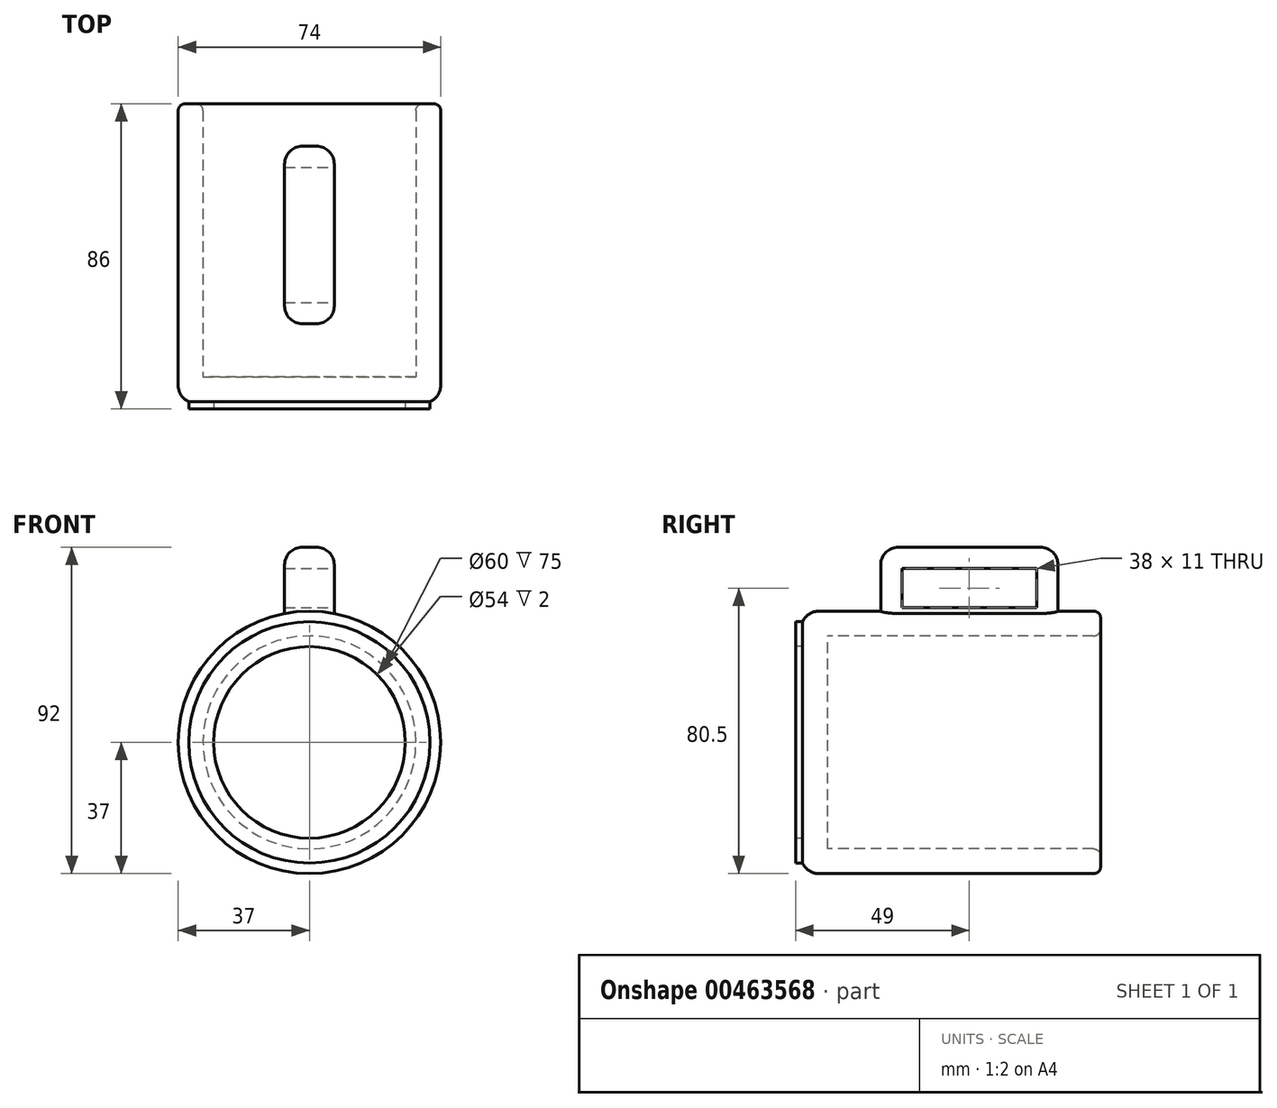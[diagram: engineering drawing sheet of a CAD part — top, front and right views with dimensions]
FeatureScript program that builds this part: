
annotation { "Feature Type Name" : "Feature", "Feature Type Description" : "" }
export const myFeature = defineFeature(function(context is Context, id is Id, definition is map)
    precondition{}
    {
        {
            var Q0;
            Q0=qCreatedBy(makeId("Top.planeOp"),FACE);
            var sketch = newSketch(context, id + "F0", { "sketchPlane" : qUnion([Q0])});
            skLineSegment(sketch, "E0", {"start": v(0, 0) * mm, "end": v(-30, 0) * mm});
            skLineSegment(sketch, "E1", {"start": v(-30, 0) * mm, "end": v(-30, 77) * mm});
            skLineSegment(sketch, "E2", {"start": v(-30, 77) * mm, "end": v(-37, 77) * mm});
            skLineSegment(sketch, "E3.0", {"start": v(-37, -7) * mm, "end": v(-37, 77) * mm});
            skLineSegment(sketch, "E3.1", {"start": v(0, -7) * mm, "end": v(-27, -7) * mm});
            skLineSegment(sketch, "E4", {"start": v(0, -7) * mm, "end": v(0, 0) * mm});
            skLineSegment(sketch, "E5", {"start": v(-37, -7) * mm, "end": v(-34, -7) * mm});
            skLineSegment(sketch, "E6", {"start": v(-34, -7) * mm, "end": v(-34, -9) * mm});
            skLineSegment(sketch, "E7", {"start": v(-34, -9) * mm, "end": v(-27, -9) * mm});
            skLineSegment(sketch, "E8", {"start": v(-27, -9) * mm, "end": v(-27, -7) * mm});
            skLineSegment(sketch, "E9.trimOffspring", {"start": v(-34, -7) * mm, "end": v(-37, -7) * mm});
            skLineSegment(sketch, "E10", {"start": v(0, 0) * mm, "end": v(0, 77) * mm});
            skSolve(sketch);
        }
        {
            var Q0;
            Q0 = qSketchRegion(id + "F0", true);
            var Q1;
            Q1=sQuery(id+"F0.wireOp",EDGE,"E10");
            revolve(context, id + "F1", {"entities" : qUnion([Q0]), "axis" : qUnion([Q1]), "revolveType" : RevolveType.FULL});
        }
        {
            var Q0;
            Q0=makeQuery(id+"F1.opRevolve","SWEPT_EDGE",EDGE,{"disambiguationData":[OSD([sQuery(id+"F0.wireOp",EDGE,"E2"),sQuery(id+"F0.wireOp",EDGE,"E3.0")])]});
            var Q1;
            Q1=makeQuery(id+"F1.opRevolve","SWEPT_EDGE",EDGE,{"disambiguationData":[OSD([sQuery(id+"F0.wireOp",EDGE,"E1"),sQuery(id+"F0.wireOp",EDGE,"E2")])]});
            fillet(context, id + "F2", {"entities" : qUnion([Q0, Q1]), "radius" : 2 * mm, "tangentPropagation" : true, "allowEdgeOverflow" : false});
        }
        {
            var Q0;
            Q0=makeQuery(id+"F1.opRevolve","SWEPT_EDGE",EDGE,{"disambiguationData":[OSD([sQuery(id+"F0.wireOp",EDGE,"E3.0"),sQuery(id+"F0.wireOp",EDGE,"E9.trimOffspring")])]});
            fillet(context, id + "F3", {"entities" : qUnion([Q0]), "radius" : 5 * mm, "tangentPropagation" : true, "allowEdgeOverflow" : false});
        }
        {
            var Q0;
            Q0=qCreatedBy(makeId("Top.planeOp"),FACE);
            cPlane(context, id + "F4", {"entities" : qUnion([Q0]), "cplaneType" : CPlaneType.OFFSET, "offset" : 35 * mm, "width" : 150 * mm, "height" : 150 * mm});
        }
        {
            var Q0;
            Q0=qCreatedBy(id+"F4.planeOp",FACE);
            var sketch = newSketch(context, id + "F5", { "sketchPlane" : qUnion([Q0])});
            skLineSegment(sketch, "E11", {"start": v(0, 0) * mm, "end": v(0, 15) * mm});
            skLineSegment(sketch, "E12", {"start": v(0, 15) * mm, "end": v(0, 65) * mm});
            skLineSegment(sketch, "E13", {"start": v(0, 65) * mm, "end": v(-7, 65) * mm});
            skLineSegment(sketch, "E14", {"start": v(0, 65) * mm, "end": v(7, 65) * mm});
            skLineSegment(sketch, "E15", {"start": v(7, 65) * mm, "end": v(7, 15) * mm});
            skLineSegment(sketch, "E16", {"start": v(7, 15) * mm, "end": v(-7, 15) * mm});
            skLineSegment(sketch, "E17", {"start": v(-7, 15) * mm, "end": v(-7, 65) * mm});
            skSolve(sketch);
        }
        {
            var Q0;
            Q0 = qSketchRegion(id + "F5", true);
            extrude(context, id + "F6", {"entities" : qUnion([Q0]), "operationType" : NewBodyOperationType.ADD, "depth" : 20 * mm});
        }
        {
            var Q0;
            Q0=makeQuery(id+"F6.opExtrude","SWEPT_FACE",FACE,{"disambiguationData":[OSD([sQuery(id+"F5.wireOp",EDGE,"E15")])]});
            var sketch = newSketch(context, id + "F7", { "sketchPlane" : qUnion([Q0])});
            skLineSegment(sketch, "E18.0", {"start": v(21, 49) * mm, "end": v(21, 38) * mm});
            skLineSegment(sketch, "E18.1", {"start": v(59, 49) * mm, "end": v(21, 49) * mm});
            skLineSegment(sketch, "E18.2", {"start": v(59, 49) * mm, "end": v(59, 38) * mm});
            skLineSegment(sketch, "E19", {"start": v(21, 38) * mm, "end": v(59, 38) * mm});
            skSolve(sketch);
        }
        {
            var Q0;
            Q0=makeQuery(id+"F6.opExtrude","CAP_EDGE",EDGE,{"disambiguationData":[OSD([sQuery(id+"F5.wireOp",EDGE,"E13"),sQuery(id+"F5.wireOp",EDGE,"E14")])],"isStart":false});
            var Q1;
            Q1=makeQuery(id+"F6.opExtrude","CAP_EDGE",EDGE,{"disambiguationData":[OSD([sQuery(id+"F5.wireOp",EDGE,"E16")])],"isStart":false});
            var Q2;
            Q2=makeQuery(id+"FSj36u2VrDCEDAY_2.boolean.opBoolean","COPY",EDGE,{"derivedFrom":makeQuery(id+"FSj36u2VrDCEDAY_2.opExtrude","SWEPT_EDGE",EDGE,{"disambiguationData":[OSD([sQuery(id+"F7.wireOp",EDGE,"E18.1"),sQuery(id+"F7.wireOp",EDGE,"E18.2")])]})});
            var Q3;
            Q3=makeQuery(id+"FSj36u2VrDCEDAY_2.boolean.opBoolean","COPY",EDGE,{"derivedFrom":makeQuery(id+"FSj36u2VrDCEDAY_2.opExtrude","SWEPT_EDGE",EDGE,{"disambiguationData":[OSD([sQuery(id+"F7.wireOp",EDGE,"E18.0"),sQuery(id+"F7.wireOp",EDGE,"E18.1")])]})});
            fillet(context, id + "F8", {"entities" : qUnion([Q0, Q1, Q2, Q3]), "radius" : 5 * mm, "tangentPropagation" : true, "allowEdgeOverflow" : false});
        }
        {
            var Q0;
            Q0 = qSketchRegion(id + "F7", true);
            extrude(context, id + "F9", {"entities" : qUnion([Q0]), "operationType" : NewBodyOperationType.REMOVE, "oppositeDirection" : true, "depth" : 25 * mm});
        }
        {
            var Q0;
            Q0=makeQuery(id+"F6.opExtrude","CAP_EDGE",EDGE,{"disambiguationData":[OSD([sQuery(id+"F5.wireOp",EDGE,"E15")])],"isStart":false});
            fillet(context, id + "F10", {"entities" : qUnion([Q0]), "radius" : 5 * mm, "tangentPropagation" : true, "allowEdgeOverflow" : false});
        }
        {
            var Q0;
            Q0=makeQuery(id+"F6.opExtrude","CAP_EDGE",EDGE,{"disambiguationData":[OSD([sQuery(id+"F5.wireOp",EDGE,"E17")])],"isStart":false});
            fillet(context, id + "F11", {"entities" : qUnion([Q0]), "radius" : 5 * mm, "tangentPropagation" : true, "allowEdgeOverflow" : false});
        }
    });
